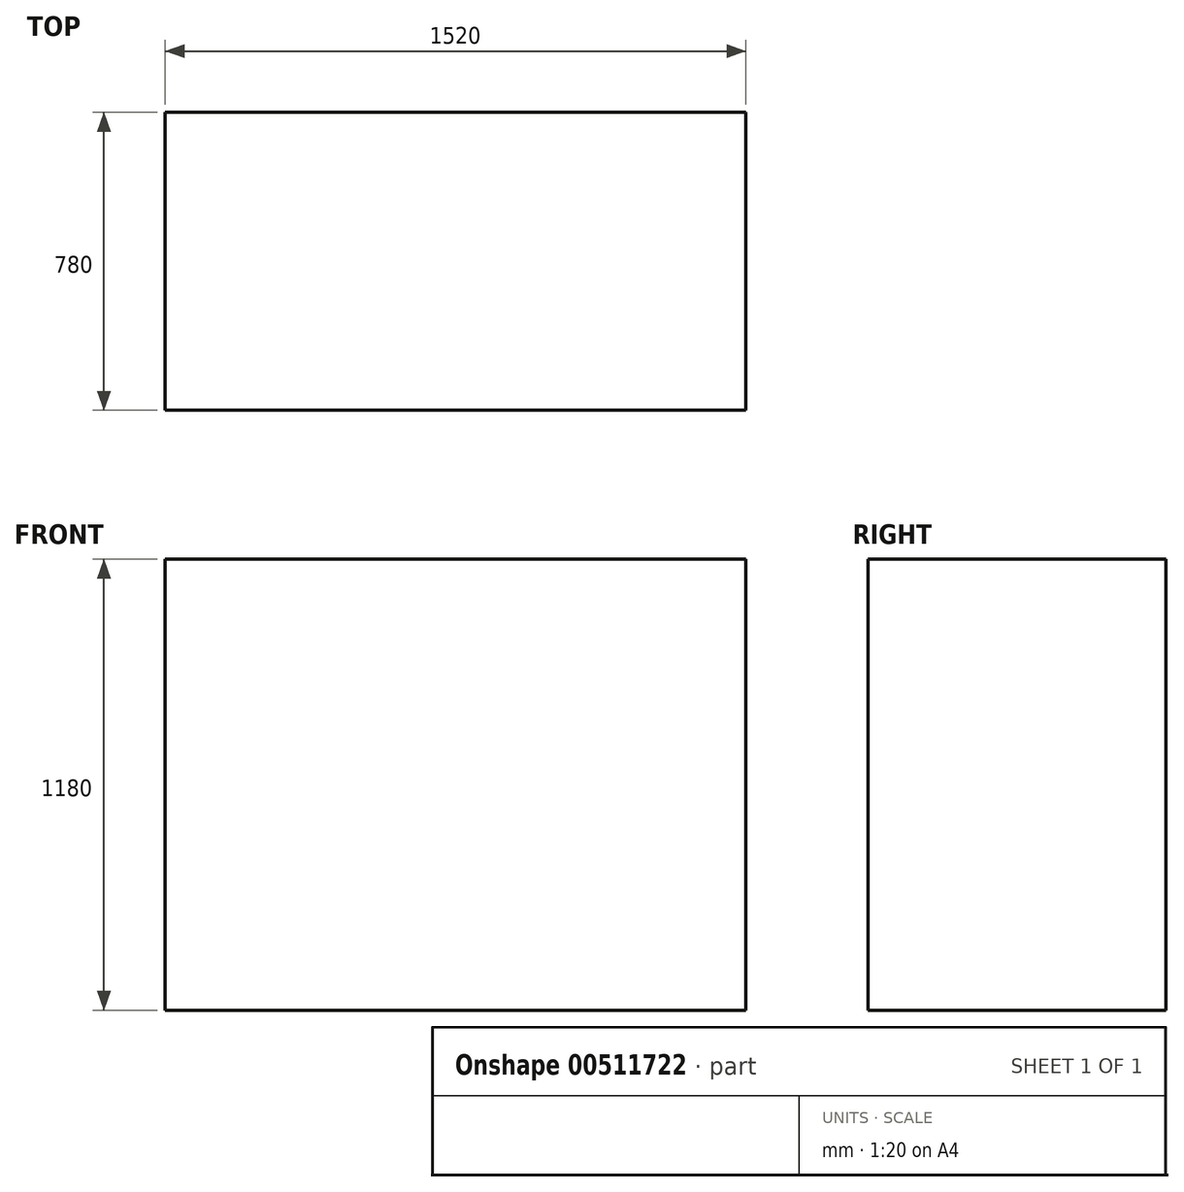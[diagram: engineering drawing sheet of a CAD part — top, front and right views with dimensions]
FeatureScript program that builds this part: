
annotation { "Feature Type Name" : "Feature", "Feature Type Description" : "" }
export const myFeature = defineFeature(function(context is Context, id is Id, definition is map)
    precondition{}
    {
        {
            var Q0;
            Q0=qCreatedBy(makeId("Top.planeOp"),FACE);
            var sketch = newSketch(context, id + "F0", { "sketchPlane" : qUnion([Q0])});
            skLineSegment(sketch, "E0.bottom", {"start": v(-640.74, 0) * mm, "end": v(879.26, 0) * mm});
            skLineSegment(sketch, "E0.top", {"start": v(-640.74, -780) * mm, "end": v(879.26, -780) * mm});
            skLineSegment(sketch, "E0.left", {"start": v(-640.74, 0) * mm, "end": v(-640.74, -780) * mm});
            skLineSegment(sketch, "E0.right", {"start": v(879.26, 0) * mm, "end": v(879.26, -780) * mm});
            skSolve(sketch);
        }
        {
            var Q0;
            Q0 = qSketchRegion(id + "F0", true);
            extrude(context, id + "F1", {"entities" : qUnion([Q0]), "depth" : 1180 * mm});
        }
    });
